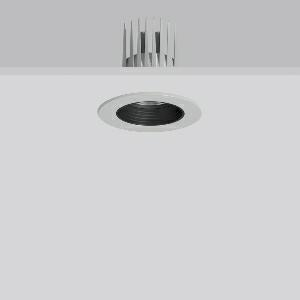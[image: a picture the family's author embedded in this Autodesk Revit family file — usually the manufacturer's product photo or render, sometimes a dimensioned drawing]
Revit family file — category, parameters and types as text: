
# Revit family: heledon_mini_e_901751_004_2_76_3a81
name_source: partatom
category: Lighting Fixtures
units: mm (PartAtom-declared; Revit-internal decimal feet)

## family parameters
Cut with Voids When Loaded = No
Host = Face
Light Source = No
Part Type = Normal
Room Calculation Point = No
Round Connector Dimension = Use Diameter
Shared = No

## types (1)
- HELEDON mini E (1 x LED Modul 927, 3000 lm, 2700)
    Apparent Load = 29 VA
    Approval mark = CE
    CIE Flux Codes = 99 100 100 100 100
    Color Rendering = 92
    Color Temperature = 2700
    Default Elevation = 1800 mm
    Description = Series: HELEDON mini
Round recessed downlight. Housing: die-cast aluminium, powder-coated. Black plastic ring and recessed LED to prevent glare from the side. Optical assembly with lens made of plastic (polycarbonate) for the best homogeneous light distribution - can be changed without tools. Best colour rendering index Ra>90. Suitable for Recessed ceiling mounting. Installation without tools thanks to spring fastening system. Including separate LED converter with connecting cable 600 mm.High quality converter without flickering and stroboscopic effect. Through-wiring box (5 pole) available as accessory. The following accessories can be mounted without use of tools: interchangeable lenses, decorative glasses, honeycomb louvre, clear and frosted diffusers, white interchangeable plastic ring. 
Colour: silver
Diameter: 124 mm
Height: 3 mm
Cut-out diameter: 114 mm
Recess height: 170 mm
Luminaire: recess height: 120 mm
Lamp: LED
Socket: without socket
Colour temperature: 2700K
Colour rendering index (CRI): 92
System power: 29 W
Rated luminous flux: 3000 lm
Luminous efficiency: 103 lm/W
Control gear: Converter, dimmable, DALI
Protection class: II
Type of protection: IP 20
    Height = 0 mm  [stored 0 ft]
    Lamp = 1 x LED Modul 927
    Lamp Light Flux = 3000 lm
    Lamp count = 1
    Length = 124 mm  [stored 0.406824 ft]
    Lifetime = 50000 h
    Luminous efficacy = 103 lm/W
    Manufacturer = RZB
    ModVariant = No
    Model = 901751.004.2.76
    Mounting Place = Ceiling
    Mounting Type = Recessed
    Number of Poles = 1
    OnlyDefault = Yes
    Power Factor = 1
    Product Name = HELEDON mini E
    Product group = Recessed downlights
    ProductGroupID = 402
    Protection Class = Protection class II
    Protection Degree = IP 20
    RLX_Detail_Level = 1
    RLX_Emergency_Light_Flux = 0 lm
    RLX_Emergency_Type = 0
    RLX_Emergency_Type_DB = No
    RlxData = <blob elided: 124317 chars, md5=1203b627>
    Socket = socket
    Standby Power = 0 W
    System Light Flux = 3000 lm
    System Power = 29 W
    Type Comments = Product without accessories
    Type Image = 901656.004.jpg
    URL = http://relux.com
    VarID = ---
    Voltage = 230 V
    Voltage Range = 220-240 V
    Weight = 0.00 kg
    Width = 0 mm  [stored 0 ft]

note: [stored X ft] marks values corroborated as IEEE doubles in the binary element streams (Revit-internal decimal feet)

## geometry (parser evidence)
native form markers: Blend x4, Sweep x10
no freeform markers — native parametric forms only
